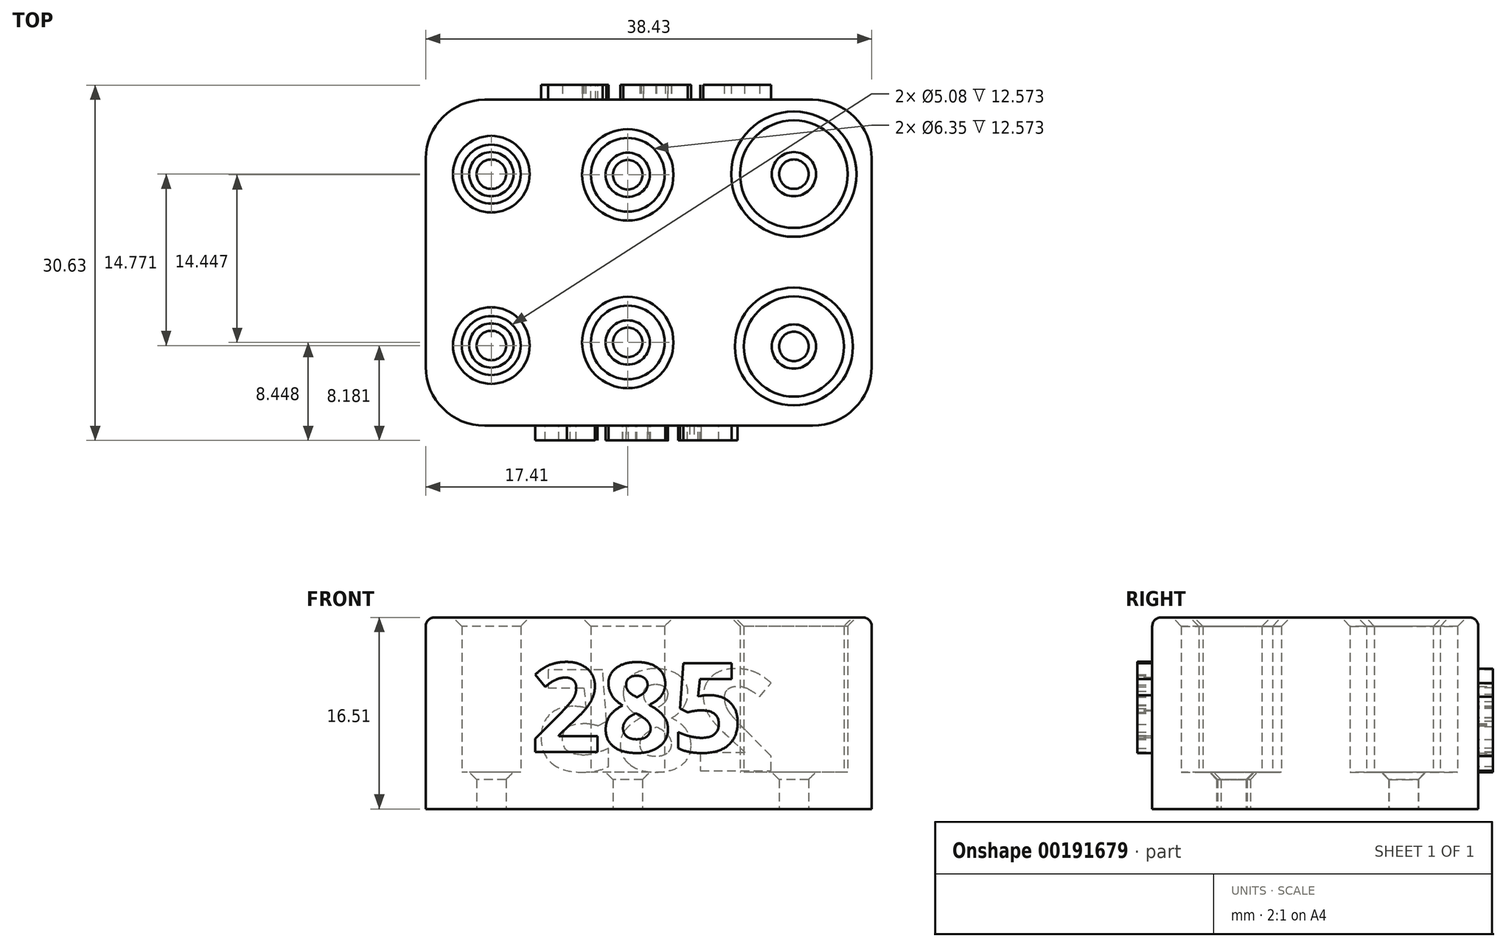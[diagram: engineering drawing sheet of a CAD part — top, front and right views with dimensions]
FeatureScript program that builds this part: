
annotation { "Feature Type Name" : "Feature", "Feature Type Description" : "" }
export const myFeature = defineFeature(function(context is Context, id is Id, definition is map)
    precondition{}
    {
        {
            var Q0;
            Q0=qCreatedBy(makeId("Top.planeOp"),FACE);
            var sketch = newSketch(context, id + "F0", { "sketchPlane" : qUnion([Q0])});
            skLineSegment(sketch, "E0.bottom", {"start": v(5.08, 0) * mm, "end": v(33.35, 0) * mm});
            skLineSegment(sketch, "E0.top", {"start": v(5.08, 28.1) * mm, "end": v(33.35, 28.1) * mm});
            skLineSegment(sketch, "E0.left", {"start": v(0, 5.08) * mm, "end": v(0, 23.01) * mm});
            skLineSegment(sketch, "E0.right", {"start": v(38.43, 5.08) * mm, "end": v(38.43, 23.01) * mm});
            skLineSegment(sketch, "E1", {"start": v(5.65, 28.1) * mm, "end": v(5.65, 0) * mm, "construction": true});
            skLineSegment(sketch, "E2", {"start": v(17.41, 28.1) * mm, "end": v(17.41, 0) * mm, "construction": true});
            skLineSegment(sketch, "E3", {"start": v(31.72, 28.1) * mm, "end": v(31.72, 0) * mm, "construction": true});
            skCircle(sketch, "E4", {"center": v(5.65, 21.68) * mm, "radius": 2.54 * mm});
            skCircle(sketch, "E5", {"center": v(5.65, 6.91) * mm, "radius": 2.54 * mm});
            skCircle(sketch, "E6", {"center": v(17.41, 21.62) * mm, "radius": 3.18 * mm});
            skCircle(sketch, "E7", {"center": v(17.41, 7.18) * mm, "radius": 3.18 * mm});
            skCircle(sketch, "E8", {"center": v(31.72, 21.68) * mm, "radius": 4.64 * mm});
            skCircle(sketch, "E9", {"center": v(31.72, 6.83) * mm, "radius": 4.32 * mm});
            skLineSegment(sketch, "E10", {"start": v(0, 21.68) * mm, "end": v(38.43, 21.68) * mm, "construction": true});
            skLineSegment(sketch, "E11", {"start": v(0, 6.91) * mm, "end": v(38.43, 6.91) * mm, "construction": true});
            skPoint(sketch, "E12.visualSharp", {"position": v(0, 28.1) * mm});
            skArc(sketch, "E12.filletArc", {"start": v(5.08, 28.1) * mm, "mid": v(1.49, 26.6) * mm, "end": v(0, 23.01) * mm});
            skPoint(sketch, "E13.visualSharp", {"position": v(38.43, 28.1) * mm});
            skArc(sketch, "E13.filletArc", {"start": v(38.43, 23.01) * mm, "mid": v(36.94, 26.6) * mm, "end": v(33.35, 28.1) * mm});
            skPoint(sketch, "E14.visualSharp", {"position": v(38.43, 0) * mm});
            skArc(sketch, "E14.filletArc", {"start": v(33.35, 0) * mm, "mid": v(36.94, 1.49) * mm, "end": v(38.43, 5.08) * mm});
            skPoint(sketch, "E15.visualSharp", {"position": v(0, 0) * mm});
            skArc(sketch, "E15.filletArc", {"start": v(0, 5.08) * mm, "mid": v(1.49, 1.49) * mm, "end": v(5.08, 0) * mm});
            skCircle(sketch, "E16", {"center": v(31.72, 21.68) * mm, "radius": 1.27 * mm});
            skCircle(sketch, "E17", {"center": v(31.72, 6.83) * mm, "radius": 1.27 * mm});
            skCircle(sketch, "E18", {"center": v(17.41, 21.62) * mm, "radius": 1.27 * mm});
            skCircle(sketch, "E19", {"center": v(17.41, 7.18) * mm, "radius": 1.27 * mm});
            skCircle(sketch, "E20", {"center": v(5.65, 6.91) * mm, "radius": 1.27 * mm});
            skCircle(sketch, "E21", {"center": v(5.65, 21.68) * mm, "radius": 1.27 * mm});
            skSolve(sketch);
        }
        {
            var Q0;
            Q0 = qSketchRegion(id + "F0", true);
            extrude(context, id + "F1", {"entities" : qUnion([Q0]), "depth" : 16.5 * mm});
        }
        {
            var Q0;
            Q0=makeQuery(id+"F0.imprint","IMPRINT",FACE,{"disambiguationData":[TD([[makeQuery(id+"F0.imprint","IMPRINT",EDGE,{"derivedFrom":sQuery(id+"F0.wireOp",EDGE,"E4")}),1.0]])]});
            var Q1;
            Q1=makeQuery(id+"F0.imprint","IMPRINT",FACE,{"disambiguationData":[TD([[makeQuery(id+"F0.imprint","IMPRINT",EDGE,{"derivedFrom":sQuery(id+"F0.wireOp",EDGE,"E6")}),1.0]])]});
            var Q2;
            Q2=makeQuery(id+"F0.imprint","IMPRINT",FACE,{"disambiguationData":[TD([[makeQuery(id+"F0.imprint","IMPRINT",EDGE,{"derivedFrom":sQuery(id+"F0.wireOp",EDGE,"E8")}),1.0]])]});
            var Q3;
            Q3=makeQuery(id+"F0.imprint","IMPRINT",FACE,{"disambiguationData":[TD([[makeQuery(id+"F0.imprint","IMPRINT",EDGE,{"derivedFrom":sQuery(id+"F0.wireOp",EDGE,"E9")}),1.0]])]});
            var Q4;
            Q4=makeQuery(id+"F0.imprint","IMPRINT",FACE,{"disambiguationData":[TD([[makeQuery(id+"F0.imprint","IMPRINT",EDGE,{"derivedFrom":sQuery(id+"F0.wireOp",EDGE,"E7")}),1.0]])]});
            var Q5;
            Q5=makeQuery(id+"F0.imprint","IMPRINT",FACE,{"disambiguationData":[TD([[makeQuery(id+"F0.imprint","IMPRINT",EDGE,{"derivedFrom":sQuery(id+"F0.wireOp",EDGE,"E5")}),1.0]])]});
            extrude(context, id + "F2", {"entities" : qUnion([Q0, Q1, Q2, Q3, Q4, Q5]), "operationType" : NewBodyOperationType.ADD, "depth" : 3.17 * mm});
        }
        {
            var Q0;
            Q0=makeQuery(id+"F1.opExtrude","CAP_EDGE",EDGE,{"disambiguationData":[OSD([sQuery(id+"F0.wireOp",EDGE,"E4")])],"isStart":false});
            var Q1;
            Q1=makeQuery(id+"F1.opExtrude","CAP_EDGE",EDGE,{"disambiguationData":[OSD([sQuery(id+"F0.wireOp",EDGE,"E6")])],"isStart":false});
            var Q2;
            Q2=makeQuery(id+"F1.opExtrude","CAP_EDGE",EDGE,{"disambiguationData":[OSD([sQuery(id+"F0.wireOp",EDGE,"E8")])],"isStart":false});
            var Q3;
            Q3=makeQuery(id+"F1.opExtrude","CAP_EDGE",EDGE,{"disambiguationData":[OSD([sQuery(id+"F0.wireOp",EDGE,"E9")])],"isStart":false});
            var Q4;
            Q4=makeQuery(id+"F1.opExtrude","CAP_EDGE",EDGE,{"disambiguationData":[OSD([sQuery(id+"F0.wireOp",EDGE,"E7")])],"isStart":false});
            var Q5;
            Q5=makeQuery(id+"F1.opExtrude","CAP_EDGE",EDGE,{"disambiguationData":[OSD([sQuery(id+"F0.wireOp",EDGE,"E5")])],"isStart":false});
            chamfer(context, id + "F3", {"entities" : qUnion([Q0, Q1, Q2, Q3, Q4, Q5]), "width" : 0.76 * mm, "tangentPropagation" : true});
        }
        {
            var Q0;
            Q0=makeQuery(id+"F1.opExtrude","CAP_EDGE",EDGE,{"disambiguationData":[OSD([sQuery(id+"F0.wireOp",EDGE,"E0.top")])],"isStart":false});
            var Q1;
            Q1=makeQuery(id+"F1.opExtrude","CAP_EDGE",EDGE,{"disambiguationData":[OSD([sQuery(id+"F0.wireOp",EDGE,"E13.filletArc")])],"isStart":false});
            var Q2;
            Q2=makeQuery(id+"F1.opExtrude","CAP_EDGE",EDGE,{"disambiguationData":[OSD([sQuery(id+"F0.wireOp",EDGE,"E0.right")])],"isStart":false});
            var Q3;
            Q3=makeQuery(id+"F1.opExtrude","CAP_EDGE",EDGE,{"disambiguationData":[OSD([sQuery(id+"F0.wireOp",EDGE,"E14.filletArc")])],"isStart":false});
            var Q4;
            Q4=makeQuery(id+"F1.opExtrude","CAP_EDGE",EDGE,{"disambiguationData":[OSD([sQuery(id+"F0.wireOp",EDGE,"E0.bottom")])],"isStart":false});
            var Q5;
            Q5=makeQuery(id+"F1.opExtrude","CAP_EDGE",EDGE,{"disambiguationData":[OSD([sQuery(id+"F0.wireOp",EDGE,"E15.filletArc")])],"isStart":false});
            var Q6;
            Q6=makeQuery(id+"F1.opExtrude","CAP_EDGE",EDGE,{"disambiguationData":[OSD([sQuery(id+"F0.wireOp",EDGE,"E0.left")])],"isStart":false});
            var Q7;
            Q7=makeQuery(id+"F1.opExtrude","CAP_EDGE",EDGE,{"disambiguationData":[OSD([sQuery(id+"F0.wireOp",EDGE,"E12.filletArc")])],"isStart":false});
            fillet(context, id + "F4", {"entities" : qUnion([Q0, Q1, Q2, Q3, Q4, Q5, Q6, Q7]), "radius" : 0.76 * mm, "tangentPropagation" : true, "allowEdgeOverflow" : false});
        }
        {
            var Q0;
            Q0=makeQuery(id+"F1.opExtrude","SWEPT_FACE",FACE,{"disambiguationData":[OSD([sQuery(id+"F0.wireOp",EDGE,"E0.bottom")])]});
            var sketch = newSketch(context, id + "F5", { "sketchPlane" : qUnion([Q0])});
            skText(sketch, "E22", { "text": "285", "fontName": "OpenSans-Bold.ttf"});
            const initialGuessF5  = {"E22": [0.00902, 0.00492, 1, 0, 0.00771]};
            skSetInitialGuess(sketch, initialGuessF5);
            skSolve(sketch);
        }
        {
            var Q0;
            Q0 = qSketchRegion(id + "F5", true);
            extrude(context, id + "F6", {"entities" : qUnion([Q0]), "operationType" : NewBodyOperationType.ADD, "depth" : 1.27 * mm});
        }
        {
            var Q0;
            Q0=makeQuery(id+"F2.opExtrude","CAP_EDGE",EDGE,{"disambiguationData":[OSD([sQuery(id+"F0.wireOp",EDGE,"E16")])],"isStart":false});
            var Q1;
            Q1=makeQuery(id+"F2.opExtrude","CAP_EDGE",EDGE,{"disambiguationData":[OSD([sQuery(id+"F0.wireOp",EDGE,"E18")])],"isStart":false});
            var Q2;
            Q2=makeQuery(id+"F2.opExtrude","CAP_EDGE",EDGE,{"disambiguationData":[OSD([sQuery(id+"F0.wireOp",EDGE,"E21")])],"isStart":false});
            var Q3;
            Q3=makeQuery(id+"F2.opExtrude","CAP_EDGE",EDGE,{"disambiguationData":[OSD([sQuery(id+"F0.wireOp",EDGE,"E20")])],"isStart":false});
            var Q4;
            Q4=makeQuery(id+"F2.opExtrude","CAP_EDGE",EDGE,{"disambiguationData":[OSD([sQuery(id+"F0.wireOp",EDGE,"E19")])],"isStart":false});
            var Q5;
            Q5=makeQuery(id+"F2.opExtrude","CAP_EDGE",EDGE,{"disambiguationData":[OSD([sQuery(id+"F0.wireOp",EDGE,"E17")])],"isStart":false});
            chamfer(context, id + "F7", {"entities" : qUnion([Q0, Q1, Q2, Q3, Q4, Q5]), "width" : 0.64 * mm, "tangentPropagation" : true});
        }
        {
            var Q0;
            Q0=makeQuery(id+"F1.opExtrude","SWEPT_FACE",FACE,{"disambiguationData":[OSD([sQuery(id+"F0.wireOp",EDGE,"E0.top")])]});
            var sketch = newSketch(context, id + "F8", { "sketchPlane" : qUnion([Q0])});
            skText(sketch, "E23", { "text": "285", "fontName": "OpenSans-Bold.ttf"});
            const initialGuessF8  = {"E23": [-0.03023, 0.00329, 1, 0, 0.00876]};
            skSetInitialGuess(sketch, initialGuessF8);
            skSolve(sketch);
        }
        {
            var Q0;
            Q0=makeQuery(id+"F8.imprint","IMPRINT",FACE,{"disambiguationData":[TD([[makeQuery(id+"F8.imprint","IMPRINT",EDGE,{"derivedFrom":sQuery(id+"F8.wireOp",EDGE,"E23.sketch_text.stroke-55")}),-1.0]])]});
            var Q1;
            Q1 = qSketchRegion(id + "F8", true);
            extrude(context, id + "F9", {"entities" : qUnion([Q0, Q1]), "operationType" : NewBodyOperationType.ADD, "depth" : 1.27 * mm});
        }
    });
